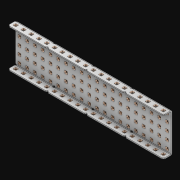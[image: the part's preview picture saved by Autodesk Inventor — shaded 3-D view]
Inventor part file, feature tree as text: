
AUTODESK INVENTOR PART (.ipt)
format: ipt  version: 2021 (Build 250183000, 183)  size: 3,380,736 bytes
history: native  units: in
note: dims shown in document units (in); Inventor stores cm internally (conversion verified against a paired STEP export)
features: extrude x141, other x140, sketch x4, thicken_offset x3, pattern_linear x3, imported_body x1
ambient origin geometry x8: Origin, YZ Plane, XZ Plane, XY Plane, X Axis, Y Axis, Z Axis, Center Point
bodies: Solid1 (feature_tree)
feature tree (292):
  thicken_offset  "Thicken1"
  thicken_offset  "Thicken2"
  thicken_offset  "Thicken3"
  pattern_linear  "Rectangular Pattern1"  Spacing1=0.001in  [1 undecoded]
  pattern_linear  "Rectangular Pattern2"  Spacing1=0.001in  [1 undecoded]
  pattern_linear  "Rectangular Pattern3"  Spacing1=0.182in  [1 undecoded]
  extrude  "Extrusion1"  Depth=0.063in TaperAngle=0.0deg
  sketch  "Sketch1"  dims[d0=0.001in]
  other  "Srf1"
  sketch  "Sketch2"  dims[d1=0.001in]
  other  "Srf2"
  sketch  "Sketch3"  dims[d2=0.001in]
  other  "Srf3"
  other  "Srf4"
  other  "Srf5"
  other  "Srf6"
  other  "Srf7"
  other  "Srf8"
  other  "Srf9"
  other  "Srf10"
  other  "Srf11"
  other  "Srf12"
  other  "Srf13"
  other  "Srf14"
  other  "Srf15"
  other  "Srf16"
  other  "Srf17"
  other  "Srf18"
  other  "Srf19"
  other  "Srf20"
  other  "Srf21"
  other  "Srf38"
  other  "Srf39"
  other  "Srf40"
  other  "Srf41"
  other  "Srf42"
  other  "Srf43"
  other  "Srf44"
  other  "Srf45"
  other  "Srf46"
  other  "Srf47"
  other  "Srf48"
  other  "Srf49"
  other  "Srf50"
  other  "Srf51"
  other  "Srf52"
  other  "Srf53"
  other  "Srf54"
  other  "Srf55"
  other  "Srf72"
  other  "Srf73"
  other  "Srf74"
  other  "Srf75"
  other  "Srf76"
  other  "Srf77"
  other  "Srf78"
  other  "Srf79"
  other  "Srf80"
  other  "Srf81"
  other  "Srf82"
  other  "Srf83"
  other  "Srf84"
  other  "Srf85"
  other  "Srf86"
  other  "Srf87"
  other  "Srf88"
  other  "Srf89"
  other  "Srf106"
  other  "Srf107"
  other  "Srf108"
  other  "Srf109"
  other  "Srf110"
  other  "Srf111"
  other  "Srf112"
  other  "Srf113"
  other  "Srf114"
  other  "Srf115"
  other  "Srf116"
  other  "Srf117"
  other  "Srf118"
  other  "Srf119"
  other  "Srf120"
  other  "Srf121"
  other  "Srf122"
  other  "Srf123"
  other  "Srf124"
  other  "Srf141"
  other  "Srf142"
  other  "Srf143"
  other  "Srf144"
  other  "Srf145"
  other  "Srf146"
  other  "Srf147"
  other  "Srf148"
  other  "Srf149"
  other  "Srf150"
  other  "Srf151"
  other  "Srf152"
  other  "Srf153"
  other  "Srf154"
  other  "Srf155"
  other  "Srf156"
  other  "Srf157"
  other  "Srf158"
  other  "Srf159"
  other  "Srf176"
  other  "Srf177"
  other  "Srf178"
  other  "Srf179"
  other  "Srf180"
  other  "Srf181"
  other  "Srf182"
  other  "Srf183"
  other  "Srf184"
  other  "Srf185"
  other  "Srf186"
  other  "Srf187"
  other  "Srf188"
  other  "Srf189"
  other  "Srf190"
  other  "Srf191"
  other  "Srf192"
  other  "Srf193"
  other  "Srf194"
  other  "Srf211"
  other  "Srf212"
  other  "Srf213"
  other  "Srf214"
  other  "Srf215"
  other  "Srf216"
  other  "Srf217"
  other  "Srf218"
  other  "Srf219"
  other  "Srf220"
  other  "Srf221"
  other  "Srf222"
  other  "Srf223"
  other  "Srf224"
  other  "Srf225"
  other  "Srf226"
  other  "Srf227"
  other  "Srf228"
  other  "Srf229"
  sketch  "Sketch4"  dims[d3=0.001in d4=0.001in d5=0.001in d6=0.182in d7=0.063in d8=0.0in d9=0.182in d10=0.063in d11=0.0in d12=0.182in d13=0.063in d14=0.0in d17=0.5in d18=7.874in d20=0.5in d21=7.874in d23=0.5in d24=1.9685in d26=0.5in d27=7.5in d28=0.0in]
  other  "Srf253"
  other  "Srf254"
  other  "Srf255"
  other  "Srf256"
  other  "Srf257"
  other  "Srf258"
  other  "Srf259"
  imported_body  "Imported1"
  extrude  "ExtrusionSrf1"  Depth=7.5in
  extrude  "ExtrusionSrf2"  Depth=0.063in TaperAngle=0.0deg
  extrude  "ExtrusionSrf3"  Depth=7.5in
  extrude  "ExtrusionSrf4"  Depth=0.063in TaperAngle=0.0deg
  extrude  "ExtrusionSrf5"  Depth=0.5in
  extrude  "ExtrusionSrf6"  Depth=7.5in
  extrude  "ExtrusionSrf7"  Depth=0.5in
  extrude  "ExtrusionSrf8"  Depth=7.5in
  extrude  "ExtrusionSrf9"  Depth=0.5in
  extrude  "ExtrusionSrf10"  Depth=0.5in
  extrude  "ExtrusionSrf11"  Depth=7.5in
  extrude  "ExtrusionSrf12"  TaperAngle=0.0deg  [1 undecoded]
  extrude  "ExtrusionSrf13"  [1 undecoded]
  extrude  "ExtrusionSrf14"  [1 undecoded]
  extrude  "ExtrusionSrf15"  [1 undecoded]
  extrude  "ExtrusionSrf16"  [1 undecoded]
  extrude  "ExtrusionSrf17"  [1 undecoded]
  extrude  "ExtrusionSrf18"  [1 undecoded]
  extrude  "ExtrusionSrf19"  [1 undecoded]
  extrude  "ExtrusionSrf20"  [1 undecoded]
  extrude  "ExtrusionSrf21"  [1 undecoded]
  extrude  "ExtrusionSrf38"  [1 undecoded]
  extrude  "ExtrusionSrf39"  [1 undecoded]
  extrude  "ExtrusionSrf40"  [1 undecoded]
  extrude  "ExtrusionSrf41"  [1 undecoded]
  extrude  "ExtrusionSrf42"  [1 undecoded]
  extrude  "ExtrusionSrf43"  [1 undecoded]
  extrude  "ExtrusionSrf44"  [1 undecoded]
  extrude  "ExtrusionSrf45"  [1 undecoded]
  extrude  "ExtrusionSrf46"  [1 undecoded]
  extrude  "ExtrusionSrf47"  [1 undecoded]
  extrude  "ExtrusionSrf48"  [1 undecoded]
  extrude  "ExtrusionSrf49"  [1 undecoded]
  extrude  "ExtrusionSrf50"  [1 undecoded]
  extrude  "ExtrusionSrf51"  [1 undecoded]
  extrude  "ExtrusionSrf52"  [1 undecoded]
  extrude  "ExtrusionSrf53"  [1 undecoded]
  extrude  "ExtrusionSrf54"  [1 undecoded]
  extrude  "ExtrusionSrf55"  [1 undecoded]
  extrude  "ExtrusionSrf72"  [1 undecoded]
  extrude  "ExtrusionSrf73"  [1 undecoded]
  extrude  "ExtrusionSrf74"  [1 undecoded]
  extrude  "ExtrusionSrf75"  [1 undecoded]
  extrude  "ExtrusionSrf76"  [1 undecoded]
  extrude  "ExtrusionSrf77"  [1 undecoded]
  extrude  "ExtrusionSrf78"  [1 undecoded]
  extrude  "ExtrusionSrf79"  [1 undecoded]
  extrude  "ExtrusionSrf80"  [1 undecoded]
  extrude  "ExtrusionSrf81"  [1 undecoded]
  extrude  "ExtrusionSrf82"  [1 undecoded]
  extrude  "ExtrusionSrf83"  [1 undecoded]
  extrude  "ExtrusionSrf84"  [1 undecoded]
  extrude  "ExtrusionSrf85"  [1 undecoded]
  extrude  "ExtrusionSrf86"  [1 undecoded]
  extrude  "ExtrusionSrf87"  [1 undecoded]
  extrude  "ExtrusionSrf88"  [1 undecoded]
  extrude  "ExtrusionSrf89"  [1 undecoded]
  extrude  "ExtrusionSrf106"  [1 undecoded]
  extrude  "ExtrusionSrf107"  [1 undecoded]
  extrude  "ExtrusionSrf108"  [1 undecoded]
  extrude  "ExtrusionSrf109"  [1 undecoded]
  extrude  "ExtrusionSrf110"  [1 undecoded]
  extrude  "ExtrusionSrf111"  [1 undecoded]
  extrude  "ExtrusionSrf112"  [1 undecoded]
  extrude  "ExtrusionSrf113"  [1 undecoded]
  extrude  "ExtrusionSrf114"  [1 undecoded]
  extrude  "ExtrusionSrf115"  [1 undecoded]
  extrude  "ExtrusionSrf116"  [1 undecoded]
  extrude  "ExtrusionSrf117"  [1 undecoded]
  extrude  "ExtrusionSrf118"  [1 undecoded]
  extrude  "ExtrusionSrf119"  [1 undecoded]
  extrude  "ExtrusionSrf120"  [1 undecoded]
  extrude  "ExtrusionSrf121"  [1 undecoded]
  extrude  "ExtrusionSrf122"  [1 undecoded]
  extrude  "ExtrusionSrf123"  [1 undecoded]
  extrude  "ExtrusionSrf124"  [1 undecoded]
  extrude  "ExtrusionSrf141"  [1 undecoded]
  extrude  "ExtrusionSrf142"  [1 undecoded]
  extrude  "ExtrusionSrf143"  [1 undecoded]
  extrude  "ExtrusionSrf144"  [1 undecoded]
  extrude  "ExtrusionSrf145"  [1 undecoded]
  extrude  "ExtrusionSrf146"  [1 undecoded]
  extrude  "ExtrusionSrf147"  [1 undecoded]
  extrude  "ExtrusionSrf148"  [1 undecoded]
  extrude  "ExtrusionSrf149"  [1 undecoded]
  extrude  "ExtrusionSrf150"  [1 undecoded]
  extrude  "ExtrusionSrf151"  [1 undecoded]
  extrude  "ExtrusionSrf152"  [1 undecoded]
  extrude  "ExtrusionSrf153"  [1 undecoded]
  extrude  "ExtrusionSrf154"  [1 undecoded]
  extrude  "ExtrusionSrf155"  [1 undecoded]
  extrude  "ExtrusionSrf156"  [1 undecoded]
  extrude  "ExtrusionSrf157"  [1 undecoded]
  extrude  "ExtrusionSrf158"  [1 undecoded]
  extrude  "ExtrusionSrf159"  [1 undecoded]
  extrude  "ExtrusionSrf176"  [1 undecoded]
  extrude  "ExtrusionSrf177"  [1 undecoded]
  extrude  "ExtrusionSrf178"  [1 undecoded]
  extrude  "ExtrusionSrf179"  [1 undecoded]
  extrude  "ExtrusionSrf180"  [1 undecoded]
  extrude  "ExtrusionSrf181"  [1 undecoded]
  extrude  "ExtrusionSrf182"  [1 undecoded]
  extrude  "ExtrusionSrf183"  [1 undecoded]
  extrude  "ExtrusionSrf184"  [1 undecoded]
  extrude  "ExtrusionSrf185"  [1 undecoded]
  extrude  "ExtrusionSrf186"  [1 undecoded]
  extrude  "ExtrusionSrf187"  [1 undecoded]
  extrude  "ExtrusionSrf188"  [1 undecoded]
  extrude  "ExtrusionSrf189"  [1 undecoded]
  extrude  "ExtrusionSrf190"  [1 undecoded]
  extrude  "ExtrusionSrf191"  [1 undecoded]
  extrude  "ExtrusionSrf192"  [1 undecoded]
  extrude  "ExtrusionSrf193"  [1 undecoded]
  extrude  "ExtrusionSrf194"  [1 undecoded]
  extrude  "ExtrusionSrf211"  [1 undecoded]
  extrude  "ExtrusionSrf212"  [1 undecoded]
  extrude  "ExtrusionSrf213"  [1 undecoded]
  extrude  "ExtrusionSrf214"  [1 undecoded]
  extrude  "ExtrusionSrf215"  [1 undecoded]
  extrude  "ExtrusionSrf216"  [1 undecoded]
  extrude  "ExtrusionSrf217"  [1 undecoded]
  extrude  "ExtrusionSrf218"  [1 undecoded]
  extrude  "ExtrusionSrf219"  [1 undecoded]
  extrude  "ExtrusionSrf220"  [1 undecoded]
  extrude  "ExtrusionSrf221"  [1 undecoded]
  extrude  "ExtrusionSrf222"  [1 undecoded]
  extrude  "ExtrusionSrf223"  [1 undecoded]
  extrude  "ExtrusionSrf224"  [1 undecoded]
  extrude  "ExtrusionSrf225"  [1 undecoded]
  extrude  "ExtrusionSrf226"  [1 undecoded]
  extrude  "ExtrusionSrf227"  [1 undecoded]
  extrude  "ExtrusionSrf228"  [1 undecoded]
  extrude  "ExtrusionSrf229"  [1 undecoded]
  extrude  "ExtrusionSrf253"  [1 undecoded]
  extrude  "ExtrusionSrf254"  [1 undecoded]
  extrude  "ExtrusionSrf255"  [1 undecoded]
  extrude  "ExtrusionSrf256"  [1 undecoded]
  extrude  "ExtrusionSrf257"  [1 undecoded]
  extrude  "ExtrusionSrf258"  [1 undecoded]
  extrude  "ExtrusionSrf259"  [1 undecoded]
note: 132 required parameter values undecoded (feature->parameter linkage not recoverable at this tier; creation-order binding heuristic only, values carry confidence <= 0.55)
